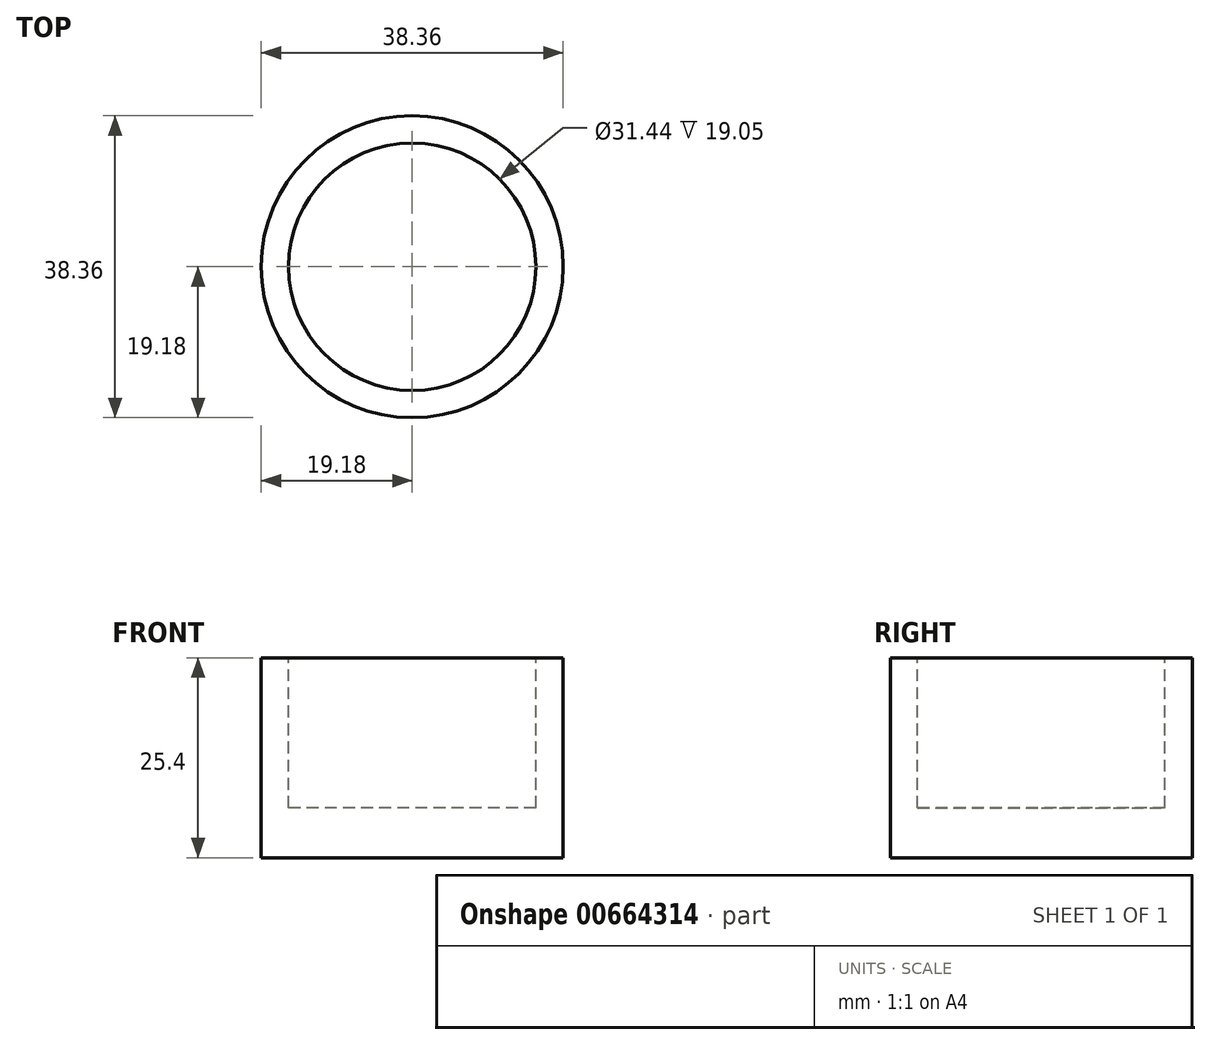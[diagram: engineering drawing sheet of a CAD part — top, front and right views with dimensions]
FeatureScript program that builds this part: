
annotation { "Feature Type Name" : "Feature", "Feature Type Description" : "" }
export const myFeature = defineFeature(function(context is Context, id is Id, definition is map)
    precondition{}
    {
        {
            var Q0;
            Q0=qCreatedBy(makeId("Top.planeOp"),FACE);
            var sketch = newSketch(context, id + "F0", { "sketchPlane" : qUnion([Q0])});
            skCircle(sketch, "E0", {"center": v(0, 0) * mm, "radius": 19.18 * mm});
            skSolve(sketch);
        }
        {
            var Q0;
            Q0=makeQuery(id+"F0.imprint","IMPRINT",FACE,{"disambiguationData":[TD([[makeQuery(id+"F0.imprint","IMPRINT",EDGE,{"derivedFrom":sQuery(id+"F0.wireOp",EDGE,"E0")}),1.0]])]});
            extrude(context, id + "F1", {"entities" : qUnion([Q0]), "depth" : 25.4 * mm, "offsetDistance" : 25.4 * mm});
        }
        {
            var Q0;
            Q0=qCreatedBy(makeId("Front.planeOp"),FACE);
            var sketch = newSketch(context, id + "F2", { "sketchPlane" : qUnion([Q0])});
            skLineSegment(sketch, "E1", {"start": v(0, 0) * mm, "end": v(0, -76.7) * mm});
            skSolve(sketch);
        }
        {
            var Q0;
            Q0=qCreatedBy(makeId("Right.planeOp"),FACE);
            var sketch = newSketch(context, id + "F3", { "sketchPlane" : qUnion([Q0])});
            skLineSegment(sketch, "E2", {"start": v(0, -76.03) * mm, "end": v(-16.9, 0) * mm});
            skSolve(sketch);
        }
        {
            var Q0;
            Q0=sQuery(id+"F3.wireOp",EDGE,"E2");
            var Q1;
            Q1=sQuery(id+"F2.wireOp",EDGE,"E1");
            revolve(context, id + "F4", {"bodyType" : ToolBodyType.SURFACE, "surfaceEntities" : qUnion([Q0]), "axis" : qUnion([Q1]), "revolveType" : RevolveType.FULL});
        }
        {
            var Q0;
            Q0=makeQuery(id+"F1.opExtrude","CAP_FACE",FACE,{"disambiguationData":[OSD([sQuery(id+"F0.wireOp",EDGE,"E0")])],"isStart":false});
            var sketch = newSketch(context, id + "F5", { "sketchPlane" : qUnion([Q0])});
            skSolve(sketch);
        }
        {
            var Q0;
            Q0=makeQuery(id+"F5.imprint","IMPRINT",FACE,{"disambiguationData":[TD([[makeQuery(id+"F5.imprint","IMPRINT",EDGE,{"derivedFrom":makeQuery(id+"F1.opExtrude","CAP_EDGE",EDGE,{"disambiguationData":[OSD([sQuery(id+"F0.wireOp",EDGE,"E0")])],"isStart":false})}),1.0]])]});
            var sketch = newSketch(context, id + "F6", { "sketchPlane" : qUnion([Q0])});
            skCircle(sketch, "E3", {"center": v(0, 0) * mm, "radius": 15.72 * mm});
            skSolve(sketch);
        }
        {
            var Q0;
            Q0=makeQuery(id+"F6.imprint","IMPRINT",FACE,{"disambiguationData":[TD([[makeQuery(id+"F6.imprint","IMPRINT",EDGE,{"derivedFrom":sQuery(id+"F6.wireOp",EDGE,"E3")}),1.0]])]});
            var Q1;
            Q1=sQuery(id+"F6.wireOp",EDGE,"E3");
            extrude(context, id + "F7", {"entities" : qUnion([Q0]), "operationType" : NewBodyOperationType.REMOVE, "surfaceEntities" : qUnion([Q1]), "oppositeDirection" : true, "depth" : 19.05 * mm, "offsetDistance" : 25.4 * mm});
        }
    });
